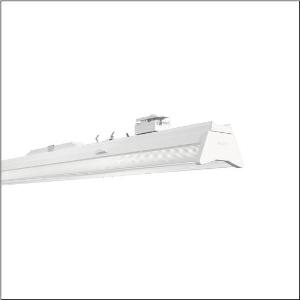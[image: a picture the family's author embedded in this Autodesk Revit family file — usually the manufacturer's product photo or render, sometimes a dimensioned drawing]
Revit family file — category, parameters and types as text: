
# Revit family: licross_r__21_performance_mo_52td167n485g_efc6
name_source: partatom
category: Lighting Fixtures
units: mm (PartAtom-declared; Revit-internal decimal feet)

## family parameters
Cut with Voids When Loaded = No
Host = Face
Light Source = No
Part Type = Normal
Room Calculation Point = No
Round Connector Dimension = Use Diameter
Shared = No

## types (1)
- Licross® 21 Performance MO (1 x LED, 8720 lm, 47.9 W, 4000K)
    Apparent Load = 48 VA
    CIE Flux Codes = 66 88 96 79 100
    Color Rendering = 80
    Color Temperature = 4000K
    Default Elevation = 1800 mm
    Description = Licross® 21 Performance MO, luminaire insert, of sheet steel, galvanised, coil coated, white, length: 1.500mm, width: 120mm, height: 123mm, LED rated luminous flux: 8.720lm, light colour: 840, control gear: ON/OFF, with plug, 3-pole, with phase selection, mains connection: 220..240V, AC, 50/60Hz, rated input power: 48W, halogen-free wiring, primary light control with lens, of plastic, primary optical cover: cover, of PMMA, light emission: direct/indirect distribution, primary light characteristic: symmetric, protection rating (complete): IP54, insulation class (complete): insulation class I (protective earthing), certification: CE, ENEC, UKCA, protection symbol: D if used in an environment with non-conductive dust loads with corresponding accessories, impact resistance: IK06, permissible ambient temperature for indoor applications: -35..+45°C, corresponds to IFS (International Featured Standards) requirements for safety and quality in the food industry, reducing of maximum allowable ambient temperature of 5°C with ceiling mounting, LABS conformity tested according to VDMA 24364:2018-05, packaging unit: 1 piece
    Height = 114 mm
    Lamp = 1 x LED
    Lamp Light Flux = 8720 lm
    Lamp Power = 47.9 W
    Lamp count = 1
    Length = 1500 mm
    Luminous efficacy = 182 lm/W
    Manufacturer = Siteco
    ModVariant = No
    Model = 52TD167N485G
    Mounting Place = Ceiling
    Mounting Type = Pendant
    Number of Poles = 1
    OnlyDefault = Yes
    Power Factor = 1
    Product Name = Licross® 21 Performance MO
    Product group = luminaire insert
    ProductGroupID = 901
    Protection Class = Protection class I
    Protection Degree = IP 54
    RLX_Detail_Level = 1
    RLX_Emergency_Light_Flux = 0 lm
    RLX_Emergency_Type = 0
    RLX_Emergency_Type_DB = No
    RlxData = <blob elided: 30345 chars, md5=3f095dff>
    Socket = socket
    Standby Power = 0 W
    System Light Flux = 8720 lm
    System Power = 48 W
    Type Comments = Product without accessories
    Type Image = l_1256138.jpg
    URL = http://relux.com
    VarID = ---
    Voltage = 0 V
    Weight = 0.00 kg
    Width = 120 mm

## geometry (parser evidence)
native form markers: Blend x4, Sweep x12
no freeform markers — native parametric forms only
